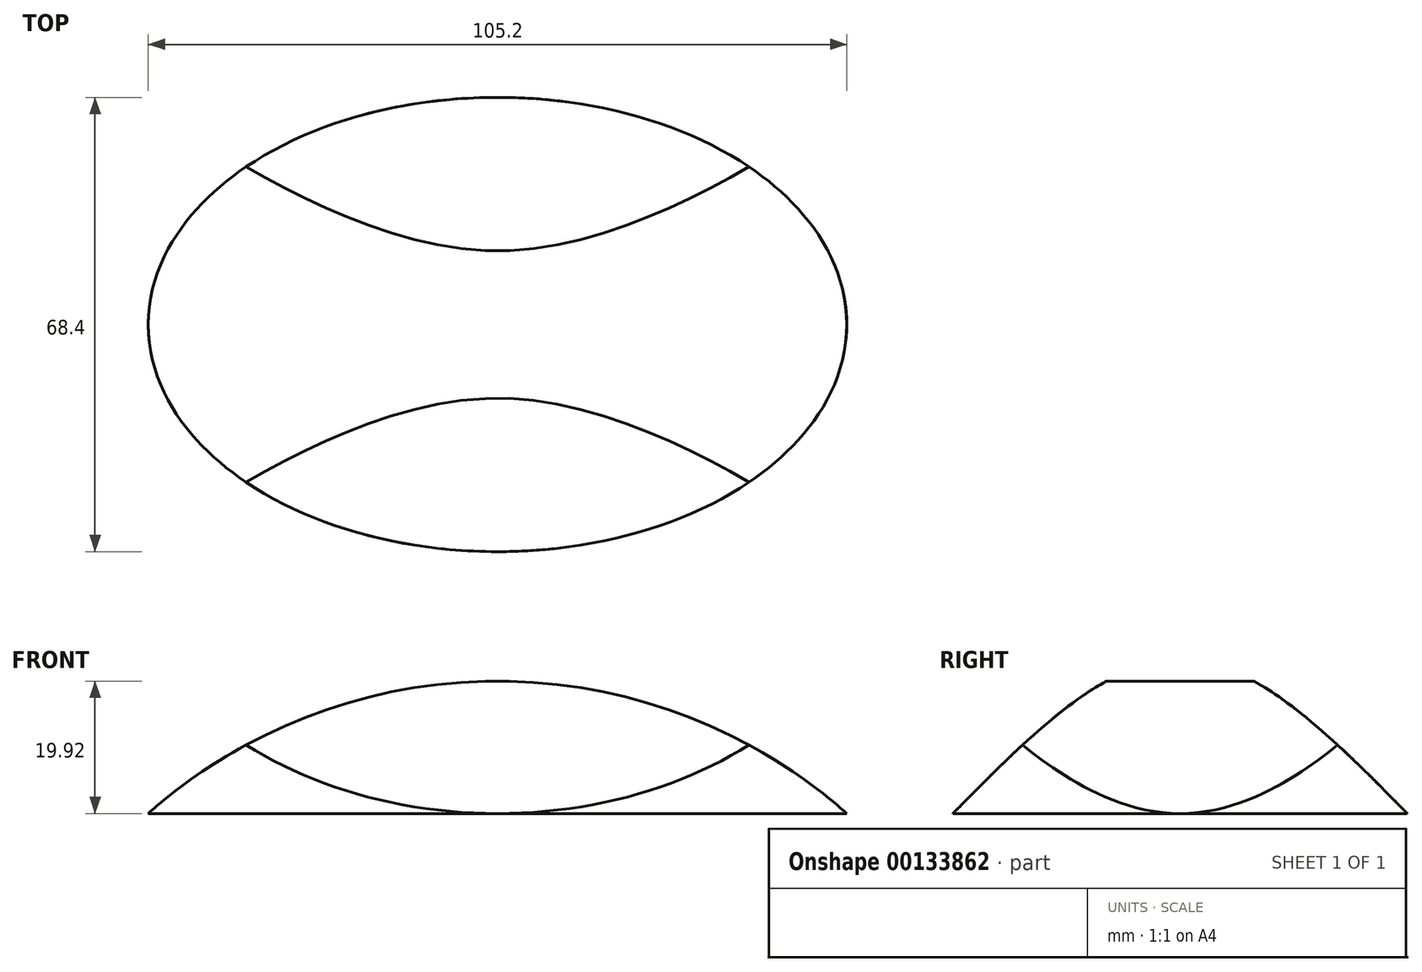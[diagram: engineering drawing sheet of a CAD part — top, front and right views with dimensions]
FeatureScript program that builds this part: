
annotation { "Feature Type Name" : "Feature", "Feature Type Description" : "" }
export const myFeature = defineFeature(function(context is Context, id is Id, definition is map)
    precondition{}
    {
        {
            var Q0;
            Q0=qCreatedBy(makeId("Top.planeOp"),FACE);
            var sketch = newSketch(context, id + "F0", { "sketchPlane" : qUnion([Q0])});
            skEllipse(sketch, "E0", {"center": v(0, 0) * mm, "majorRadius": 52.6 * mm, "minorRadius": 34.2 * mm, "majorAxis": v(1, 0)});
            skSolve(sketch);
        }
        {
            var Q0;
            Q0=makeQuery(id+"F0.imprint","IMPRINT",FACE,{"disambiguationData":[TD([[makeQuery(id+"F0.imprint","IMPRINT",EDGE,{"derivedFrom":sQuery(id+"F0.wireOp",EDGE,"E0")}),1.0]])]});
            extrude(context, id + "F1", {"entities" : qUnion([Q0]), "depth" : 25 * mm});
        }
        {
            var Q0;
            Q0=qCreatedBy(makeId("Right.planeOp"),FACE);
            var sketch = newSketch(context, id + "F2", { "sketchPlane" : qUnion([Q0])});
            skLineSegment(sketch, "E1.0", {"start": v(-34.2, 0) * mm, "end": v(34.2, 0) * mm});
            skFitSpline(sketch, "E2", {"points": [v(34.2, 0) * mm, v(0, 23.2) * mm, v(-34.2, 0) * mm], "startDerivative": vector(-68.4, 69.57) * mm, "endDerivative": vector(-68.4, -69.57) * mm});
            skSolve(sketch);
        }
        {
            var Q0;
            Q0 = qSketchRegion(id + "F2", true);
            extrude(context, id + "F3", {"entities" : qUnion([Q0]), "operationType" : NewBodyOperationType.INTERSECT, "depth" : 116.14 * mm, "symmetric" : true});
        }
        {
            var Q0;
            Q0=qCreatedBy(makeId("Front.planeOp"),FACE);
            var sketch = newSketch(context, id + "F4", { "sketchPlane" : qUnion([Q0])});
            skLineSegment(sketch, "E3", {"start": v(52.6, 0) * mm, "end": v(52.6, 0) * mm});
            skLineSegment(sketch, "E4.0", {"start": v(0, 0) * mm, "end": v(52.6, 0) * mm});
            skArc(sketch, "E5", {"start": v(52.6, 0) * mm, "mid": v(0, 19.92) * mm, "end": v(-52.6, 0) * mm});
            skLineSegment(sketch, "E6.0", {"start": v(0, 0) * mm, "end": v(-52.6, 0) * mm});
            skSolve(sketch);
        }
        {
            var Q0;
            Q0 = qSketchRegion(id + "F4", true);
            extrude(context, id + "F5", {"entities" : qUnion([Q0]), "operationType" : NewBodyOperationType.INTERSECT, "depth" : 92.85 * mm, "symmetric" : true});
        }
    });
